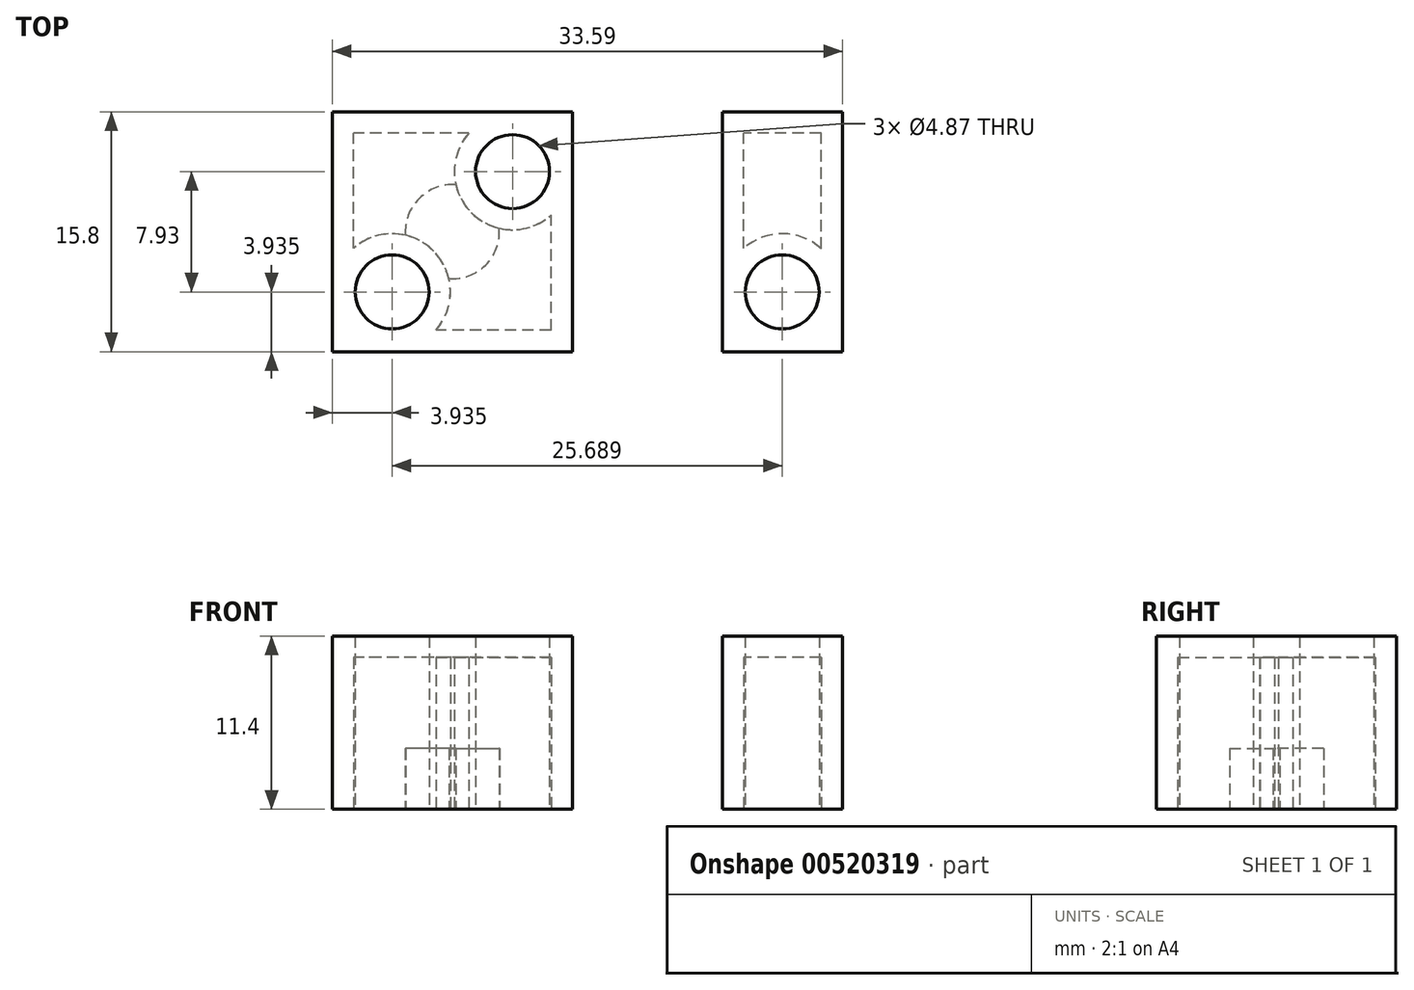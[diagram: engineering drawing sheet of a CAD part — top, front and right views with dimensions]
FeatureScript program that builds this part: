
annotation { "Feature Type Name" : "Feature", "Feature Type Description" : "" }
export const myFeature = defineFeature(function(context is Context, id is Id, definition is map)
    precondition{}
    {
        {
            var Q0;
            Q0=qCreatedBy(makeId("Top.planeOp"),FACE);
            var sketch = newSketch(context, id + "F0", { "sketchPlane" : qUnion([Q0])});
            skLineSegment(sketch, "E0.bottom", {"start": v(7.9, -7.9) * mm, "end": v(-7.9, -7.9) * mm});
            skLineSegment(sketch, "E0.top", {"start": v(7.9, 7.9) * mm, "end": v(-7.9, 7.9) * mm});
            skLineSegment(sketch, "E0.left", {"start": v(7.9, -7.9) * mm, "end": v(7.9, 7.9) * mm});
            skLineSegment(sketch, "E0.right", {"start": v(-7.9, -7.9) * mm, "end": v(-7.9, 7.9) * mm});
            skPoint(sketch, "E1.end.orphan", {"position": v(-7.9, 0) * mm});
            skPoint(sketch, "E2.orphan", {"position": v(0, 7.9) * mm});
            skPoint(sketch, "E3.end.orphan", {"position": v(0, -7.9) * mm});
            skLineSegment(sketch, "E4", {"start": v(-7.9, 7.9) * mm, "end": v(-7.9, 0) * mm});
            skCircle(sketch, "E5", {"center": v(-3.97, 3.97) * mm, "radius": 2.44 * mm});
            skCircle(sketch, "E6.MirrorC", {"center": v(3.97, 3.97) * mm, "radius": 2.44 * mm});
            skCircle(sketch, "E7.MirrorC", {"center": v(-3.97, -3.97) * mm, "radius": 2.44 * mm});
            skCircle(sketch, "E8.MirrorC", {"center": v(3.97, -3.97) * mm, "radius": 2.44 * mm});
            skPoint(sketch, "E9.end.orphan", {"position": v(7.9, 0) * mm});
            skSolve(sketch);
        }
        {
            var Q0;
            Q0 = qSketchRegion(id + "F0", true);
            extrude(context, id + "F1", {"entities" : qUnion([Q0]), "depth" : 9.6 * mm, "offsetDistance" : 25 * mm});
        }
        {
            var Q0;
            Q0=makeQuery(id+"F0.imprint","IMPRINT",FACE,{"disambiguationData":[TD([[makeQuery(id+"F0.imprint","IMPRINT",EDGE,{"derivedFrom":sQuery(id+"F0.wireOp",EDGE,"E5")}),1.0]])]});
            var Q1;
            Q1=makeQuery(id+"F0.imprint","IMPRINT",FACE,{"disambiguationData":[TD([[makeQuery(id+"F0.imprint","IMPRINT",EDGE,{"derivedFrom":sQuery(id+"F0.wireOp",EDGE,"E6.MirrorC")}),-1.0]])]});
            var Q2;
            Q2=makeQuery(id+"F0.imprint","IMPRINT",FACE,{"disambiguationData":[TD([[makeQuery(id+"F0.imprint","IMPRINT",EDGE,{"derivedFrom":sQuery(id+"F0.wireOp",EDGE,"E8.MirrorC")}),1.0]])]});
            var Q3;
            Q3=makeQuery(id+"F0.imprint","IMPRINT",FACE,{"disambiguationData":[TD([[makeQuery(id+"F0.imprint","IMPRINT",EDGE,{"derivedFrom":sQuery(id+"F0.wireOp",EDGE,"E7.MirrorC")}),-1.0]])]});
            extrude(context, id + "F2", {"entities" : qUnion([Q0, Q1, Q2, Q3]), "operationType" : NewBodyOperationType.ADD, "depth" : 11.4 * mm, "offsetDistance" : 25 * mm});
        }
        {
            var Q0;
            Q0=qCreatedBy(makeId("Top.planeOp"),FACE);
            var sketch = newSketch(context, id + "F3", { "sketchPlane" : qUnion([Q0])});
            skLineSegment(sketch, "E10.bottom", {"start": v(25.69, -7.9) * mm, "end": v(17.79, -7.9) * mm});
            skLineSegment(sketch, "E10.top", {"start": v(25.69, 7.9) * mm, "end": v(17.79, 7.9) * mm});
            skLineSegment(sketch, "E10.left", {"start": v(25.69, -7.9) * mm, "end": v(25.69, 7.9) * mm});
            skLineSegment(sketch, "E10.right", {"start": v(17.79, -7.9) * mm, "end": v(17.79, 7.9) * mm});
            skPoint(sketch, "E10.middle", {"position": v(21.74, 0) * mm});
            skCircle(sketch, "E11", {"center": v(21.72, 3.96) * mm, "radius": 2.44 * mm});
            skCircle(sketch, "E12.MirrorC", {"center": v(21.72, -3.96) * mm, "radius": 2.44 * mm});
            skPoint(sketch, "E13.orphan", {"position": v(17.79, 0) * mm});
            skPoint(sketch, "E14.end.orphan", {"position": v(25.69, 0) * mm});
            skSolve(sketch);
        }
        {
            var Q0;
            Q0 = qSketchRegion(id + "F3", true);
            extrude(context, id + "F4", {"entities" : qUnion([Q0]), "depth" : 9.6 * mm, "offsetDistance" : 25 * mm});
        }
        {
            var Q0;
            Q0=makeQuery(id+"F3.imprint","IMPRINT",FACE,{"disambiguationData":[TD([[makeQuery(id+"F3.imprint","IMPRINT",EDGE,{"derivedFrom":sQuery(id+"F3.wireOp",EDGE,"E11")}),1.0]])]});
            var Q1;
            Q1=makeQuery(id+"F3.imprint","IMPRINT",FACE,{"disambiguationData":[TD([[makeQuery(id+"F3.imprint","IMPRINT",EDGE,{"derivedFrom":sQuery(id+"F3.wireOp",EDGE,"E12.MirrorC")}),-1.0]])]});
            extrude(context, id + "F5", {"entities" : qUnion([Q0, Q1]), "operationType" : NewBodyOperationType.ADD, "depth" : 11.4 * mm, "offsetDistance" : 25 * mm});
        }
        {
            var Q0;
            {var subQ0=sQuery(id+"F0.wireOp",EDGE,"E8.MirrorC");var subQ1=sQuery(id+"F0.wireOp",EDGE,"E7.MirrorC");var subQ2=sQuery(id+"F0.wireOp",EDGE,"E6.MirrorC");var subQ3=sQuery(id+"F0.wireOp",EDGE,"E5");Q0=makeQuery(id+"F2.boolean.opBoolean","MERGE",FACE,{"derivedFrom":[makeQuery(id+"F1.opExtrude","CAP_FACE",FACE,{"disambiguationData":[OSD([sQuery(id+"F0.wireOp",EDGE,"E0.bottom"),sQuery(id+"F0.wireOp",EDGE,"E0.top"),sQuery(id+"F0.wireOp",EDGE,"E0.left"),sQuery(id+"F0.wireOp",EDGE,"E0.right"),sQuery(id+"F0.wireOp",EDGE,"E4"),subQ3,subQ2,subQ1,subQ0])],"isStart":true}),makeQuery(id+"F2.opExtrude","CAP_FACE",FACE,{"disambiguationData":[OSD([subQ3])],"isStart":true}),makeQuery(id+"F2.opExtrude","CAP_FACE",FACE,{"disambiguationData":[OSD([subQ2])],"isStart":true}),makeQuery(id+"F2.opExtrude","CAP_FACE",FACE,{"disambiguationData":[OSD([subQ1])],"isStart":true}),makeQuery(id+"F2.opExtrude","CAP_FACE",FACE,{"disambiguationData":[OSD([subQ0])],"isStart":true})]});}
            var Q1;
            Q1=makeQuery(id+"F1.opExtrude","SWEPT_BODY",BODY,{"disambiguationData":[OSD([sQuery(id+"F0.wireOp",EDGE,"E0.bottom"),sQuery(id+"F0.wireOp",EDGE,"E0.top"),sQuery(id+"F0.wireOp",EDGE,"E0.left"),sQuery(id+"F0.wireOp",EDGE,"E0.right"),sQuery(id+"F0.wireOp",EDGE,"E4"),sQuery(id+"F0.wireOp",EDGE,"E5"),sQuery(id+"F0.wireOp",EDGE,"E6.MirrorC"),sQuery(id+"F0.wireOp",EDGE,"E7.MirrorC"),sQuery(id+"F0.wireOp",EDGE,"E8.MirrorC")])]});
            shell(context, id + "F6", {"entities" : qUnion([Q0]), "parts" : qUnion([Q1]), "thickness" : 1.4 * mm});
        }
        {
            var Q0;
            {var subQ0=sQuery(id+"F3.wireOp",EDGE,"E12.MirrorC");var subQ1=sQuery(id+"F3.wireOp",EDGE,"E11");Q0=makeQuery(id+"F5.boolean.opBoolean","MERGE",FACE,{"derivedFrom":[makeQuery(id+"F4.opExtrude","CAP_FACE",FACE,{"disambiguationData":[OSD([sQuery(id+"F3.wireOp",EDGE,"E10.bottom"),sQuery(id+"F3.wireOp",EDGE,"E10.top"),sQuery(id+"F3.wireOp",EDGE,"E10.left"),sQuery(id+"F3.wireOp",EDGE,"E10.right"),subQ1,subQ0])],"isStart":true}),makeQuery(id+"F5.opExtrude","CAP_FACE",FACE,{"disambiguationData":[OSD([subQ1])],"isStart":true}),makeQuery(id+"F5.opExtrude","CAP_FACE",FACE,{"disambiguationData":[OSD([subQ0])],"isStart":true})]});}
            shell(context, id + "F7", {"entities" : qUnion([Q0]), "thickness" : 1.4 * mm});
        }
        {
            var Q0;
            Q0=qCreatedBy(makeId("Top.planeOp"),FACE);
            var sketch = newSketch(context, id + "F8", { "sketchPlane" : qUnion([Q0])});
            skCircle(sketch, "E15", {"center": v(0, 0) * mm, "radius": 3.1 * mm});
            skSolve(sketch);
        }
        {
            var Q0;
            Q0=makeQuery(id+"F8.imprint","IMPRINT",FACE,{"disambiguationData":[TD([[makeQuery(id+"F8.imprint","IMPRINT",EDGE,{"derivedFrom":sQuery(id+"F8.wireOp",EDGE,"E15")}),1.0]])]});
            extrude(context, id + "F9", {"entities" : qUnion([Q0]), "operationType" : NewBodyOperationType.ADD, "depth" : 4 * mm, "offsetDistance" : 25 * mm});
        }
    });
